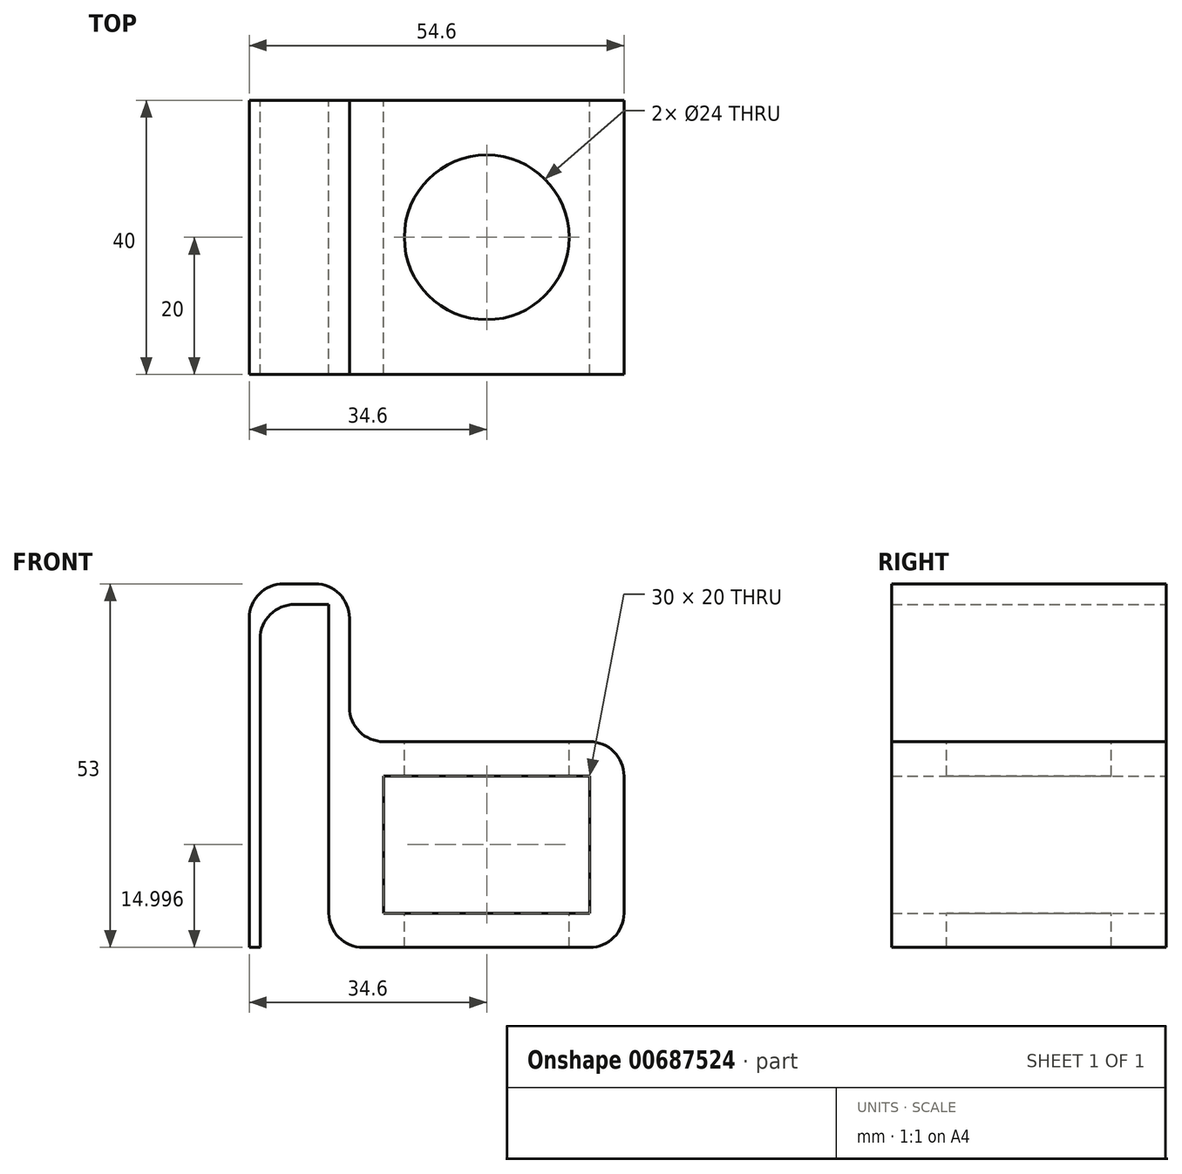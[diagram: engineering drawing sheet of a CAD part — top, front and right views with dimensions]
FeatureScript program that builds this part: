
annotation { "Feature Type Name" : "Feature", "Feature Type Description" : "" }
export const myFeature = defineFeature(function(context is Context, id is Id, definition is map)
    precondition{}
    {
        {
            var Q0;
            Q0=qCreatedBy(makeId("Front.planeOp"),FACE);
            var sketch = newSketch(context, id + "F0", { "sketchPlane" : qUnion([Q0])});
            skLineSegment(sketch, "E0.bottom", {"start": v(-5, 58.04) * mm, "end": v(-6.6, 58.04) * mm});
            skLineSegment(sketch, "E0.top", {"start": v(-5, 8.04) * mm, "end": v(-6.6, 8.04) * mm});
            skLineSegment(sketch, "E0.left", {"start": v(-5, 58.04) * mm, "end": v(-5, 8.04) * mm});
            skLineSegment(sketch, "E0.right", {"start": v(-6.6, 58.04) * mm, "end": v(-6.6, 8.04) * mm});
            skLineSegment(sketch, "E1.bottom", {"start": v(-6.6, 58.04) * mm, "end": v(5, 58.04) * mm});
            skLineSegment(sketch, "E1.top", {"start": v(-6.6, 61.04) * mm, "end": v(5, 61.04) * mm});
            skLineSegment(sketch, "E1.left", {"start": v(-6.6, 58.04) * mm, "end": v(-6.6, 61.04) * mm});
            skLineSegment(sketch, "E1.right", {"start": v(5, 58.04) * mm, "end": v(5, 61.04) * mm});
            skLineSegment(sketch, "E2.bottom", {"start": v(5, 61.04) * mm, "end": v(8, 61.04) * mm});
            skLineSegment(sketch, "E2.top", {"start": v(5, 8.04) * mm, "end": v(8, 8.04) * mm});
            skLineSegment(sketch, "E2.left", {"start": v(5, 61.04) * mm, "end": v(5, 8.04) * mm});
            skLineSegment(sketch, "E2.right", {"start": v(8, 61.04) * mm, "end": v(8, 8.04) * mm});
            skLineSegment(sketch, "E3.bottom", {"start": v(8, 8.04) * mm, "end": v(48, 8.04) * mm});
            skLineSegment(sketch, "E3.top", {"start": v(8, 38.04) * mm, "end": v(48, 38.04) * mm});
            skLineSegment(sketch, "E3.left", {"start": v(8, 8.04) * mm, "end": v(8, 38.04) * mm});
            skLineSegment(sketch, "E3.right", {"start": v(48, 8.04) * mm, "end": v(48, 38.04) * mm});
            skLineSegment(sketch, "E4.bottom", {"start": v(13, 13.04) * mm, "end": v(43, 13.04) * mm});
            skLineSegment(sketch, "E4.top", {"start": v(13, 33.04) * mm, "end": v(43, 33.04) * mm});
            skLineSegment(sketch, "E4.left", {"start": v(13, 13.04) * mm, "end": v(13, 33.04) * mm});
            skLineSegment(sketch, "E4.right", {"start": v(43, 13.04) * mm, "end": v(43, 33.04) * mm});
            skSolve(sketch);
        }
        {
            var Q0;
            Q0 = qSketchRegion(id + "F0", true);
            extrude(context, id + "F1", {"entities" : qUnion([Q0]), "endBound" : BoundingType.SYMMETRIC, "depth" : 40 * mm, "offsetDistance" : 25 * mm});
        }
        {
            var Q0;
            Q0=makeQuery(id+"F1.opExtrude","SWEPT_FACE",FACE,{"disambiguationData":[OSD([sQuery(id+"F0.wireOp",EDGE,"E3.top")])]});
            var sketch = newSketch(context, id + "F2", { "sketchPlane" : qUnion([Q0])});
            skPoint(sketch, "E5", {"position": v(28, 0) * mm});
            skPoint(sketch, "E5.positionSnap0", {"position": v(28, -20) * mm});
            skSolve(sketch);
        }
        {
            var Q0;
            Q0=sQuery(id+"F2.wireOp",VERTEX,"E5");
            var Q1;
            Q1=makeQuery(id+"F1.opExtrude","SWEPT_BODY",BODY,{"disambiguationData":[OSD([sQuery(id+"F0.wireOp",EDGE,"E0.top"),sQuery(id+"F0.wireOp",EDGE,"E0.left"),sQuery(id+"F0.wireOp",EDGE,"E0.right"),sQuery(id+"F0.wireOp",EDGE,"E1.bottom"),sQuery(id+"F0.wireOp",EDGE,"E1.top"),sQuery(id+"F0.wireOp",EDGE,"E1.left"),sQuery(id+"F0.wireOp",EDGE,"E2.bottom"),sQuery(id+"F0.wireOp",EDGE,"E2.top"),sQuery(id+"F0.wireOp",EDGE,"E2.left"),sQuery(id+"F0.wireOp",EDGE,"E2.right"),sQuery(id+"F0.wireOp",EDGE,"E3.bottom"),sQuery(id+"F0.wireOp",EDGE,"E3.top"),sQuery(id+"F0.wireOp",EDGE,"E3.right"),sQuery(id+"F0.wireOp",EDGE,"E4.bottom"),sQuery(id+"F0.wireOp",EDGE,"E4.top"),sQuery(id+"F0.wireOp",EDGE,"E4.left"),sQuery(id+"F0.wireOp",EDGE,"E4.right")])]});
            hole(context, id + "F3", {"style" : HoleStyle.SIMPLE, "endStyle" : HoleEndStyle.THROUGH, "standardTappedOrClearance" : lookupTablePath({ "fit" : "Loose", "standard" : "ISO", "size" : "M20", "type" : "Clearance" }), "standardBlindInLast" : lookupTablePath({ "fit" : "Loose", "standard" : "ISO", "size" : "M20", "type" : "Clearance" }), "holeDiameter" : 24 * mm, "majorDiameter" : 5 * mm, "isTappedThrough" : true, "tappedDepth" : 12 * mm, "tapClearance" : 3, "locations" : qUnion([Q0]), "scope" : qUnion([Q1])});
        }
        {
            var Q0;
            Q0=makeQuery(id+"F1.opExtrude","SWEPT_EDGE",EDGE,{"disambiguationData":[OSD([sQuery(id+"F0.wireOp",EDGE,"E0.left"),sQuery(id+"F0.wireOp",EDGE,"E1.bottom")])]});
            var Q1;
            Q1=makeQuery(id+"F1.opExtrude","SWEPT_EDGE",EDGE,{"disambiguationData":[OSD([sQuery(id+"F0.wireOp",EDGE,"E2.right"),sQuery(id+"F0.wireOp",EDGE,"E3.top"),sQuery(id+"F0.wireOp",EDGE,"E3.left")])]});
            var Q2;
            Q2=makeQuery(id+"F1.opExtrude","SWEPT_EDGE",EDGE,{"disambiguationData":[OSD([sQuery(id+"F0.wireOp",EDGE,"E2.bottom"),sQuery(id+"F0.wireOp",EDGE,"E2.right")])]});
            var Q3;
            Q3=makeQuery(id+"F1.opExtrude","SWEPT_EDGE",EDGE,{"disambiguationData":[OSD([sQuery(id+"F0.wireOp",EDGE,"E1.top"),sQuery(id+"F0.wireOp",EDGE,"E1.left")])]});
            var Q4;
            Q4=makeQuery(id+"F1.opExtrude","SWEPT_EDGE",EDGE,{"disambiguationData":[OSD([sQuery(id+"F0.wireOp",EDGE,"E3.top"),sQuery(id+"F0.wireOp",EDGE,"E3.right")])]});
            var Q5;
            Q5=makeQuery(id+"F1.opExtrude","SWEPT_EDGE",EDGE,{"disambiguationData":[OSD([sQuery(id+"F0.wireOp",EDGE,"E3.bottom"),sQuery(id+"F0.wireOp",EDGE,"E3.right")])]});
            var Q6;
            Q6=makeQuery(id+"F1.opExtrude","SWEPT_EDGE",EDGE,{"disambiguationData":[OSD([sQuery(id+"F0.wireOp",EDGE,"E2.top"),sQuery(id+"F0.wireOp",EDGE,"E2.left")])]});
            fillet(context, id + "F4", {"entities" : qUnion([Q0, Q1, Q2, Q3, Q4, Q5, Q6]), "radius" : 5 * mm, "tangentPropagation" : true, "allowEdgeOverflow" : false});
        }
    });
